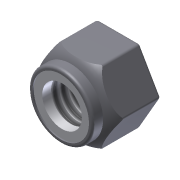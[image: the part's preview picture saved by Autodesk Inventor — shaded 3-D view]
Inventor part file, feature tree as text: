
AUTODESK INVENTOR PART (.ipt)
format: ipt  version: 2013 (Build 170138000, 138)  size: 189,952 bytes
history: native  units: in
note: dims shown in document units (in); Inventor stores cm internally (conversion verified against a paired STEP export)
features: sketch x5, extrude x3, fillet x2, hole x1, revolve x1, projected_geometry x1
ambient origin geometry x8: Origin, YZ Plane, XZ Plane, XY Plane, X Axis, Y Axis, Z Axis, Center Point
bodies: Solid1 (feature_tree)
feature tree (13):
  extrude  "Extrusion1"  Depth=0.375in TaperAngle=0.0deg
  extrude  "Extrusion2"  Depth=0.0781in TaperAngle=0.0deg
  extrude  "Extrusion3"  Depth=0.01in TaperAngle=0.0deg
  hole  "Hole2"  [1 undecoded]
  revolve  "Revolution2"  [1 undecoded]
  fillet  "Fillet1"  Radius=0.02in
  fillet  "Fillet2"  Radius=0.4062in
  sketch  "Sketch1"  dims[d0=0.5625in d1=0.375in d2=0.0in]
  sketch  "Sketch3"  dims[d3=0.5in d4=0.0781in d5=0.0in]
  sketch  "Sketch8"  dims[d14=0.4375in d15=0.01in d16=0.0in]
  sketch  "Sketch9"  dims[d17=0.307in d18=0.375in d19=0.375in d20=0.25in d21=0.5635in d22=1.0in d23=0.8108in d24=0.18in]
  sketch  "Sketch10"  dims[d25=90.0deg d26=0.02in d27=0.02in d28=0.4062in]
  projected_geometry  "Projected Loop8"
note: 2 required parameter values undecoded (feature->parameter linkage not recoverable at this tier; creation-order binding heuristic only, values carry confidence <= 0.55)